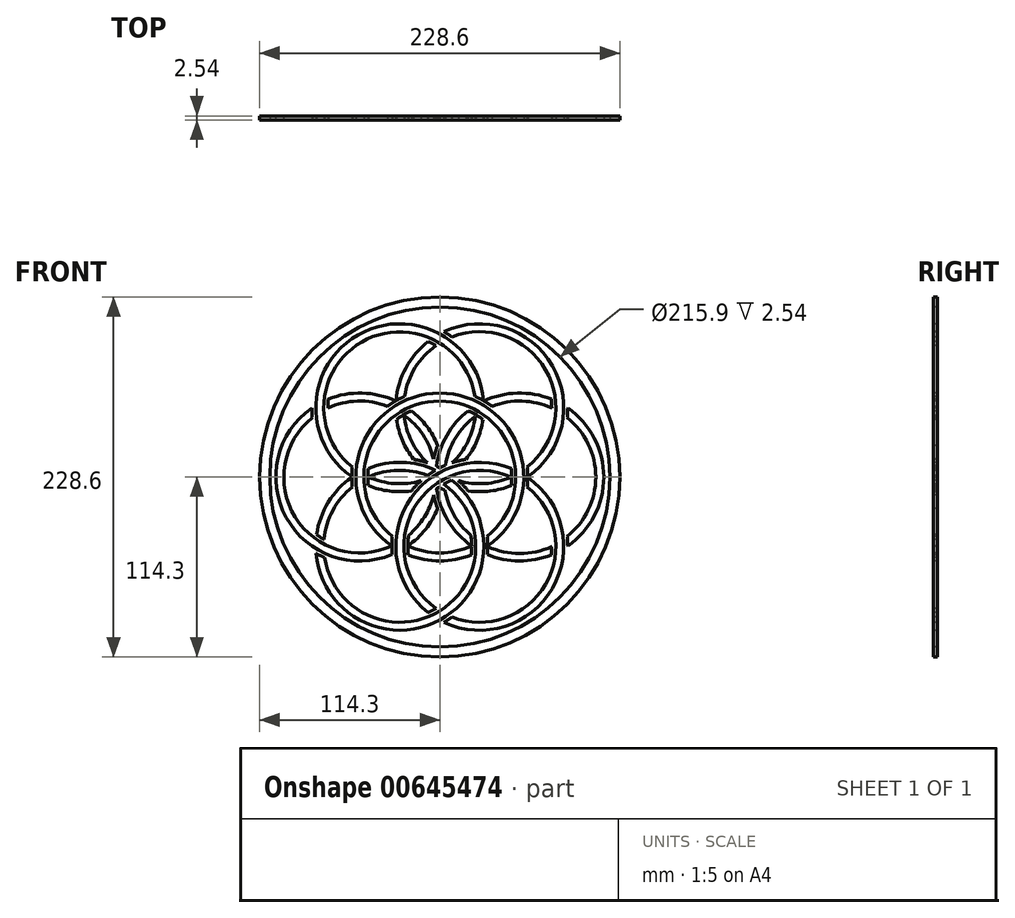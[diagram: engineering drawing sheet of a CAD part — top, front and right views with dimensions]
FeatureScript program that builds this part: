
annotation { "Feature Type Name" : "Feature", "Feature Type Description" : "" }
export const myFeature = defineFeature(function(context is Context, id is Id, definition is map)
    precondition{}
    {
        {
            var Q0;
            Q0=qCreatedBy(makeId("Front.planeOp"),FACE);
            var sketch = newSketch(context, id + "F0", { "sketchPlane" : qUnion([Q0])});
            skPoint(sketch, "E0.middle", {"position": v(0, 0) * mm});
            skCircle(sketch, "E1", {"center": v(0, 0) * mm, "radius": 114.3 * mm});
            skCircle(sketch, "E2", {"center": v(0, 0) * mm, "radius": 107.95 * mm});
            skSolve(sketch);
        }
        {
            var Q0;
            Q0=qSketchRegion(id+"F0",true);
            extrude(context, id + "F1", {"entities" : qUnion([Q0]), "depth" : -2.54 * mm, "offsetDistance" : 25.4 * mm});
        }
        {
            var Q0;
            Q0=qCreatedBy(makeId("Front.planeOp"),FACE);
            var sketch = newSketch(context, id + "F2", { "sketchPlane" : qUnion([Q0])});
            skCircle(sketch, "E3", {"center": v(0, 0) * mm, "radius": 101.6 * mm, "construction": true});
            skLineSegment(sketch, "E4", {"start": v(-101.6, 0) * mm, "end": v(101.6, 0) * mm, "construction": true});
            skLineSegment(sketch, "E5", {"start": v(50.8, 87.99) * mm, "end": v(-50.8, -87.99) * mm, "construction": true});
            skLineSegment(sketch, "E6", {"start": v(-50.8, 87.99) * mm, "end": v(50.8, -87.99) * mm, "construction": true});
            skCircle(sketch, "E7", {"center": v(0, 0) * mm, "radius": 50.8 * mm, "construction": true});
            skCircle(sketch, "E8", {"center": v(-25.4, 44) * mm, "radius": 50.8 * mm, "construction": true});
            skCircle(sketch, "E9", {"center": v(25.4, 44) * mm, "radius": 50.8 * mm, "construction": true});
            skCircle(sketch, "E10", {"center": v(50.8, 0) * mm, "radius": 50.8 * mm, "construction": true});
            skCircle(sketch, "E11", {"center": v(25.4, -44) * mm, "radius": 50.8 * mm, "construction": true});
            skCircle(sketch, "E12", {"center": v(-25.4, -44) * mm, "radius": 50.8 * mm, "construction": true});
            skCircle(sketch, "E13", {"center": v(-50.8, 0) * mm, "radius": 50.8 * mm, "construction": true});
            skArc(sketch, "E14", {"start": v(-30.12, -37.7) * mm, "mid": v(0, 48.26) * mm, "end": v(30.12, -37.7) * mm});
            skArc(sketch, "E15", {"start": v(-55.52, 6.3) * mm, "mid": v(-49.53, 85.79) * mm, "end": v(22.31, 51.23) * mm});
            skArc(sketch, "E16", {"start": v(2.35, -4.51) * mm, "mid": v(0, -85.03) * mm, "end": v(-73.11, -51.23) * mm});
            skPoint(sketch, "E16.startSnap0", {"position": v(0, 48.26) * mm});
            skArc(sketch, "E17", {"start": v(-80.92, 37.7) * mm, "mid": v(-91.83, -25.4) * mm, "end": v(-30.48, -43.77) * mm});
            skArc(sketch, "E18", {"start": v(-81.28, 43.77) * mm, "mid": v(-97.56, -25.67) * mm, "end": v(-30.24, -49.22) * mm});
            skArc(sketch, "E19", {"start": v(-30.48, -43.77) * mm, "mid": v(0, 53.34) * mm, "end": v(30.48, -43.77) * mm});
            skArc(sketch, "E20", {"start": v(7.43, -1.95) * mm, "mid": v(0, -90.9) * mm, "end": v(-78.55, -48.5) * mm});
            skArc(sketch, "E21", {"start": v(-55.88, 0.22) * mm, "mid": v(-52.07, 90.19) * mm, "end": v(27.75, 48.5) * mm});
            skArc(sketch, "E22", {"start": v(7.81, 88.93) * mm, "mid": v(67.2, 68.12) * mm, "end": v(55.52, 6.3) * mm});
            skArc(sketch, "E23", {"start": v(2.73, 92.28) * mm, "mid": v(71.6, 70.66) * mm, "end": v(55.88, 0.22) * mm});
            skArc(sketch, "E24", {"start": v(-2.35, 83.48) * mm, "mid": v(-15.63, 69.4) * mm, "end": v(-22.31, 51.23) * mm});
            skArc(sketch, "E25", {"start": v(-7.43, 86.03) * mm, "mid": v(-21.5, 69.39) * mm, "end": v(-27.75, 48.5) * mm});
            skArc(sketch, "E26", {"start": v(-71.12, 43.77) * mm, "mid": v(-52.28, 48.24) * mm, "end": v(-33.21, 44.94) * mm});
            skArc(sketch, "E27", {"start": v(-70.8, 49.45) * mm, "mid": v(-49.34, 53.32) * mm, "end": v(-28.13, 48.28) * mm});
            skArc(sketch, "E28", {"start": v(81.28, -43.77) * mm, "mid": v(104.14, 0) * mm, "end": v(81.28, 43.77) * mm});
            skArc(sketch, "E29", {"start": v(80.92, 37.7) * mm, "mid": v(99.06, 0) * mm, "end": v(80.92, -37.7) * mm});
            skArc(sketch, "E30", {"start": v(45.4, 5.46) * mm, "mid": v(-20.8, -17.32) * mm, "end": v(-7.43, -86.03) * mm});
            skArc(sketch, "E31", {"start": v(-2.35, -83.48) * mm, "mid": v(-16.4, -19.86) * mm, "end": v(45.72, -0.22) * mm});
            skArc(sketch, "E32", {"start": v(55.52, -6.3) * mm, "mid": v(67.2, -68.12) * mm, "end": v(7.81, -88.93) * mm});
            skArc(sketch, "E33", {"start": v(55.88, -0.22) * mm, "mid": v(71.6, -70.66) * mm, "end": v(2.73, -92.28) * mm});
            skCircle(sketch, "E34", {"center": v(0, 0) * mm, "radius": 55.88 * mm, "construction": true});
            skCircle(sketch, "E35", {"center": v(-50.8, 0) * mm, "radius": 55.88 * mm, "construction": true});
            skCircle(sketch, "E36", {"center": v(25.4, -44) * mm, "radius": 55.88 * mm, "construction": true});
            skCircle(sketch, "E37", {"center": v(-25.4, 44) * mm, "radius": 55.88 * mm, "construction": true});
            skCircle(sketch, "E38", {"center": v(50.8, 0) * mm, "radius": 55.88 * mm, "construction": true});
            skCircle(sketch, "E39", {"center": v(-25.4, -44) * mm, "radius": 55.88 * mm, "construction": true});
            skCircle(sketch, "E40", {"center": v(25.4, 44) * mm, "radius": 55.88 * mm, "construction": true});
            skArc(sketch, "E41", {"start": v(81.28, 43.77) * mm, "mid": v(81.18, 40.73) * mm, "end": v(80.92, 37.7) * mm});
            skArc(sketch, "E42", {"start": v(-81.28, 43.77) * mm, "mid": v(-81.18, 40.73) * mm, "end": v(-80.92, 37.7) * mm});
            skArc(sketch, "E43", {"start": v(-33.21, 44.94) * mm, "mid": v(-30.72, 46.68) * mm, "end": v(-28.13, 48.28) * mm});
            skArc(sketch, "E44", {"start": v(-22.31, 51.23) * mm, "mid": v(-25.07, 49.94) * mm, "end": v(-27.75, 48.5) * mm});
            skArc(sketch, "E45", {"start": v(55.52, 6.3) * mm, "mid": v(55.78, 3.26) * mm, "end": v(55.88, 0.22) * mm});
            skArc(sketch, "E46", {"start": v(55.52, -6.3) * mm, "mid": v(55.78, -3.26) * mm, "end": v(55.88, -0.22) * mm});
            skArc(sketch, "E47", {"start": v(22.31, 51.23) * mm, "mid": v(25.07, 49.94) * mm, "end": v(27.75, 48.5) * mm});
            skArc(sketch, "E48", {"start": v(-55.52, 6.3) * mm, "mid": v(-55.78, 3.26) * mm, "end": v(-55.88, 0.22) * mm});
            skArc(sketch, "E49", {"start": v(-30.12, -37.7) * mm, "mid": v(-30.38, -40.73) * mm, "end": v(-30.48, -43.77) * mm});
            skArc(sketch, "E50", {"start": v(30.12, -37.7) * mm, "mid": v(30.38, -40.73) * mm, "end": v(30.48, -43.77) * mm});
            skArc(sketch, "E51", {"start": v(-30.24, -49.22) * mm, "mid": v(-30.42, -46.5) * mm, "end": v(-30.48, -43.77) * mm});
            skCircle(sketch, "E52", {"center": v(-25.4, 44) * mm, "radius": 45.72 * mm, "construction": true});
            skCircle(sketch, "E53", {"center": v(0, 0) * mm, "radius": 45.72 * mm, "construction": true});
            skCircle(sketch, "E54", {"center": v(25.4, 44) * mm, "radius": 45.72 * mm, "construction": true});
            skCircle(sketch, "E55", {"center": v(50.8, 0) * mm, "radius": 45.72 * mm, "construction": true});
            skCircle(sketch, "E56", {"center": v(25.4, -44) * mm, "radius": 45.72 * mm, "construction": true});
            skCircle(sketch, "E57", {"center": v(-25.4, -44) * mm, "radius": 45.72 * mm, "construction": true});
            skCircle(sketch, "E58", {"center": v(-50.8, 0) * mm, "radius": 45.72 * mm, "construction": true});
            skArc(sketch, "E59", {"start": v(-70.8, 49.45) * mm, "mid": v(-71.04, 46.62) * mm, "end": v(-71.12, 43.77) * mm});
            skArc(sketch, "E60", {"start": v(-7.43, 86.03) * mm, "mid": v(-4.85, 84.84) * mm, "end": v(-2.35, 83.48) * mm});
            skArc(sketch, "E61", {"start": v(2.73, 92.28) * mm, "mid": v(5.32, 90.67) * mm, "end": v(7.81, 88.93) * mm});
            skArc(sketch, "E62", {"start": v(-73.11, -51.23) * mm, "mid": v(-75.87, -49.94) * mm, "end": v(-78.55, -48.5) * mm});
            skArc(sketch, "E63", {"start": v(-7.43, -86.03) * mm, "mid": v(-4.85, -84.84) * mm, "end": v(-2.35, -83.48) * mm});
            skArc(sketch, "E64", {"start": v(7.81, -88.93) * mm, "mid": v(5.32, -90.67) * mm, "end": v(2.73, -92.28) * mm});
            skArc(sketch, "E65", {"start": v(80.92, -37.7) * mm, "mid": v(81.18, -40.73) * mm, "end": v(81.28, -43.77) * mm});
            skArc(sketch, "E66", {"start": v(45.4, 5.46) * mm, "mid": v(45.64, 2.62) * mm, "end": v(45.72, -0.22) * mm});
            skArc(sketch, "E67", {"start": v(-55.52, -6.3) * mm, "mid": v(-67.92, -21.16) * mm, "end": v(-73.47, -39.7) * mm});
            skArc(sketch, "E68", {"start": v(-78.22, -36.58) * mm, "mid": v(-70.85, -16.07) * mm, "end": v(-55.88, -0.22) * mm});
            skArc(sketch, "E69", {"start": v(-45.4, 5.46) * mm, "mid": v(-23.94, 9.33) * mm, "end": v(-2.73, 4.29) * mm});
            skArc(sketch, "E70", {"start": v(-45.72, -0.22) * mm, "mid": v(-26.88, 4.24) * mm, "end": v(-7.81, 0.95) * mm});
            skArc(sketch, "E71", {"start": v(-73.47, -39.7) * mm, "mid": v(-75.9, -38.22) * mm, "end": v(-78.22, -36.58) * mm});
            skArc(sketch, "E72", {"start": v(-55.52, -6.3) * mm, "mid": v(-55.78, -3.26) * mm, "end": v(-55.88, -0.22) * mm});
            skArc(sketch, "E73", {"start": v(-45.72, -0.22) * mm, "mid": v(-45.64, 2.62) * mm, "end": v(-45.4, 5.46) * mm});
            skArc(sketch, "E74", {"start": v(-7.81, 0.95) * mm, "mid": v(-5.32, 2.69) * mm, "end": v(-2.73, 4.29) * mm});
            skArc(sketch, "E75", {"start": v(7.43, -1.95) * mm, "mid": v(4.85, -3.15) * mm, "end": v(2.35, -4.51) * mm});
            skArc(sketch, "E76", {"start": v(33.21, 44.94) * mm, "mid": v(52.28, 48.24) * mm, "end": v(71.12, 43.77) * mm});
            skArc(sketch, "E77", {"start": v(70.8, 49.45) * mm, "mid": v(49.34, 53.32) * mm, "end": v(28.13, 48.28) * mm});
            skArc(sketch, "E78", {"start": v(17.97, 42.04) * mm, "mid": v(4.45, 26.4) * mm, "end": v(-2.1, 6.8) * mm});
            skArc(sketch, "E79", {"start": v(23.54, 39.2) * mm, "mid": v(10.36, 25.37) * mm, "end": v(3.65, 7.48) * mm});
            skPoint(sketch, "E79.startSnap0", {"position": v(14.62, 39.2) * mm});
            skArc(sketch, "E80", {"start": v(-20.32, -43.7) * mm, "mid": v(0, -48.19) * mm, "end": v(20.32, -43.7) * mm});
            skArc(sketch, "E81", {"start": v(-20, -49.45) * mm, "mid": v(0, -53.34) * mm, "end": v(20, -49.45) * mm});
            skArc(sketch, "E82", {"start": v(20.32, -43.77) * mm, "mid": v(5.35, -27.92) * mm, "end": v(-2.02, -7.41) * mm});
            skArc(sketch, "E83", {"start": v(71.12, -44.18) * mm, "mid": v(50.8, -48.63) * mm, "end": v(30.48, -44.18) * mm});
            skArc(sketch, "E84", {"start": v(70.8, -49.45) * mm, "mid": v(50.5, -53.34) * mm, "end": v(30.24, -49.22) * mm});
            skArc(sketch, "E85", {"start": v(-19.78, -36.97) * mm, "mid": v(-9.8, -25.45) * mm, "end": v(-3.9, -11.4) * mm});
            skArc(sketch, "E86", {"start": v(-20.32, -43.77) * mm, "mid": v(-9.12, -33.28) * mm, "end": v(-1.37, -20.03) * mm});
            skArc(sketch, "E87", {"start": v(-22.68, 39.7) * mm, "mid": v(-18.1, 23.06) * mm, "end": v(-7.95, 9.1) * mm});
            skArc(sketch, "E88", {"start": v(-27.42, 36.58) * mm, "mid": v(-23.71, 23.18) * mm, "end": v(-16.67, 11.2) * mm});
            skArc(sketch, "E89", {"start": v(45.72, 0.22) * mm, "mid": v(29, -4.13) * mm, "end": v(11.82, -2.32) * mm});
            skArc(sketch, "E90", {"start": v(45.4, -5.46) * mm, "mid": v(31.93, -8.94) * mm, "end": v(18.03, -8.83) * mm});
            skArc(sketch, "E91", {"start": v(27.42, 36.58) * mm, "mid": v(23.71, 23.18) * mm, "end": v(16.67, 11.2) * mm});
            skArc(sketch, "E92", {"start": v(22.67, 39.7) * mm, "mid": v(18.08, 23.05) * mm, "end": v(7.92, 9.08) * mm});
            skArc(sketch, "E93", {"start": v(-45.72, 0.22) * mm, "mid": v(-29, -4.13) * mm, "end": v(-11.82, -2.32) * mm});
            skArc(sketch, "E94", {"start": v(-45.4, -5.46) * mm, "mid": v(-31.93, -8.94) * mm, "end": v(-18.03, -8.83) * mm});
            skArc(sketch, "E95", {"start": v(71.12, -44.18) * mm, "mid": v(71.03, -46.82) * mm, "end": v(70.8, -49.45) * mm});
            skArc(sketch, "E96", {"start": v(30.24, -49.22) * mm, "mid": v(30.41, -46.7) * mm, "end": v(30.48, -44.18) * mm});
            skArc(sketch, "E97", {"start": v(28.13, 48.28) * mm, "mid": v(30.72, 46.68) * mm, "end": v(33.21, 44.94) * mm});
            skArc(sketch, "E98", {"start": v(70.8, 49.45) * mm, "mid": v(71.04, 46.62) * mm, "end": v(71.12, 43.77) * mm});
            skArc(sketch, "E99", {"start": v(-27.42, 36.58) * mm, "mid": v(-25.1, 38.21) * mm, "end": v(-22.68, 39.7) * mm});
            skArc(sketch, "E100", {"start": v(-16.67, 11.2) * mm, "mid": v(-12.26, 10.32) * mm, "end": v(-7.95, 9.1) * mm});
            skArc(sketch, "E101", {"start": v(-20.32, -43.7) * mm, "mid": v(-20.25, -46.58) * mm, "end": v(-20, -49.45) * mm});
            skArc(sketch, "E102", {"start": v(20.32, -43.7) * mm, "mid": v(20.25, -46.58) * mm, "end": v(20, -49.45) * mm});
            skArc(sketch, "E103", {"start": v(-3.9, -11.4) * mm, "mid": v(-2.8, -15.77) * mm, "end": v(-1.37, -20.03) * mm});
            skArc(sketch, "E104", {"start": v(-19.78, -36.97) * mm, "mid": v(-20.18, -40.36) * mm, "end": v(-20.32, -43.77) * mm});
            skArc(sketch, "E105", {"start": v(19.78, -36.97) * mm, "mid": v(9, -24.13) * mm, "end": v(3.27, -8.38) * mm});
            skArc(sketch, "E106", {"start": v(-23.05, 39.48) * mm, "mid": v(-10.92, 27.18) * mm, "end": v(-3.9, 11.4) * mm});
            skArc(sketch, "E107", {"start": v(-1.37, 20.03) * mm, "mid": v(-8.22, 32.13) * mm, "end": v(-17.97, 42.04) * mm});
            skArc(sketch, "E108", {"start": v(-3.9, 11.4) * mm, "mid": v(-2.8, 15.77) * mm, "end": v(-1.37, 20.03) * mm});
            skArc(sketch, "E109", {"start": v(-17.97, 42.04) * mm, "mid": v(-20.55, 40.84) * mm, "end": v(-23.05, 39.48) * mm});
            skArc(sketch, "E110", {"start": v(17.97, 42.04) * mm, "mid": v(20.8, 40.71) * mm, "end": v(23.54, 39.2) * mm});
            skArc(sketch, "E111", {"start": v(27.42, 36.58) * mm, "mid": v(25.1, 38.22) * mm, "end": v(22.67, 39.7) * mm});
            skArc(sketch, "E112", {"start": v(-45.4, -5.46) * mm, "mid": v(-45.64, -2.62) * mm, "end": v(-45.72, 0.22) * mm});
            skArc(sketch, "E113", {"start": v(-11.82, -2.32) * mm, "mid": v(-15.06, -5.45) * mm, "end": v(-18.03, -8.83) * mm});
            skArc(sketch, "E114", {"start": v(19.78, -36.97) * mm, "mid": v(20.18, -40.36) * mm, "end": v(20.32, -43.77) * mm});
            skArc(sketch, "E115", {"start": v(45.4, -5.46) * mm, "mid": v(45.63, -2.84) * mm, "end": v(45.72, -0.22) * mm});
            skArc(sketch, "E116", {"start": v(11.82, -2.32) * mm, "mid": v(15.06, -5.45) * mm, "end": v(18.03, -8.83) * mm});
            skArc(sketch, "E117", {"start": v(7.92, 9.08) * mm, "mid": v(12.25, 10.32) * mm, "end": v(16.67, 11.2) * mm});
            skArc(sketch, "E118", {"start": v(3.27, -8.38) * mm, "mid": v(1.24, -7.48) * mm, "end": v(-0.75, -6.5) * mm});
            skArc(sketch, "E119", {"start": v(-0.75, -6.5) * mm, "mid": v(-1.4, -6.95) * mm, "end": v(-2.02, -7.41) * mm});
            skArc(sketch, "E120", {"start": v(-2.1, 6.8) * mm, "mid": v(-1.05, 6.3) * mm, "end": v(0, 5.78) * mm});
            skArc(sketch, "E121", {"start": v(3.65, 7.48) * mm, "mid": v(1.8, 6.66) * mm, "end": v(0, 5.78) * mm});
            skSolve(sketch);
        }
        {
            var Q0;
            Q0=qSketchRegion(id+"F2",true);
            extrude(context, id + "F3", {"entities" : qUnion([Q0]), "oppositeDirection" : true, "depth" : 2.54 * mm, "offsetDistance" : 25.4 * mm});
        }
    });
